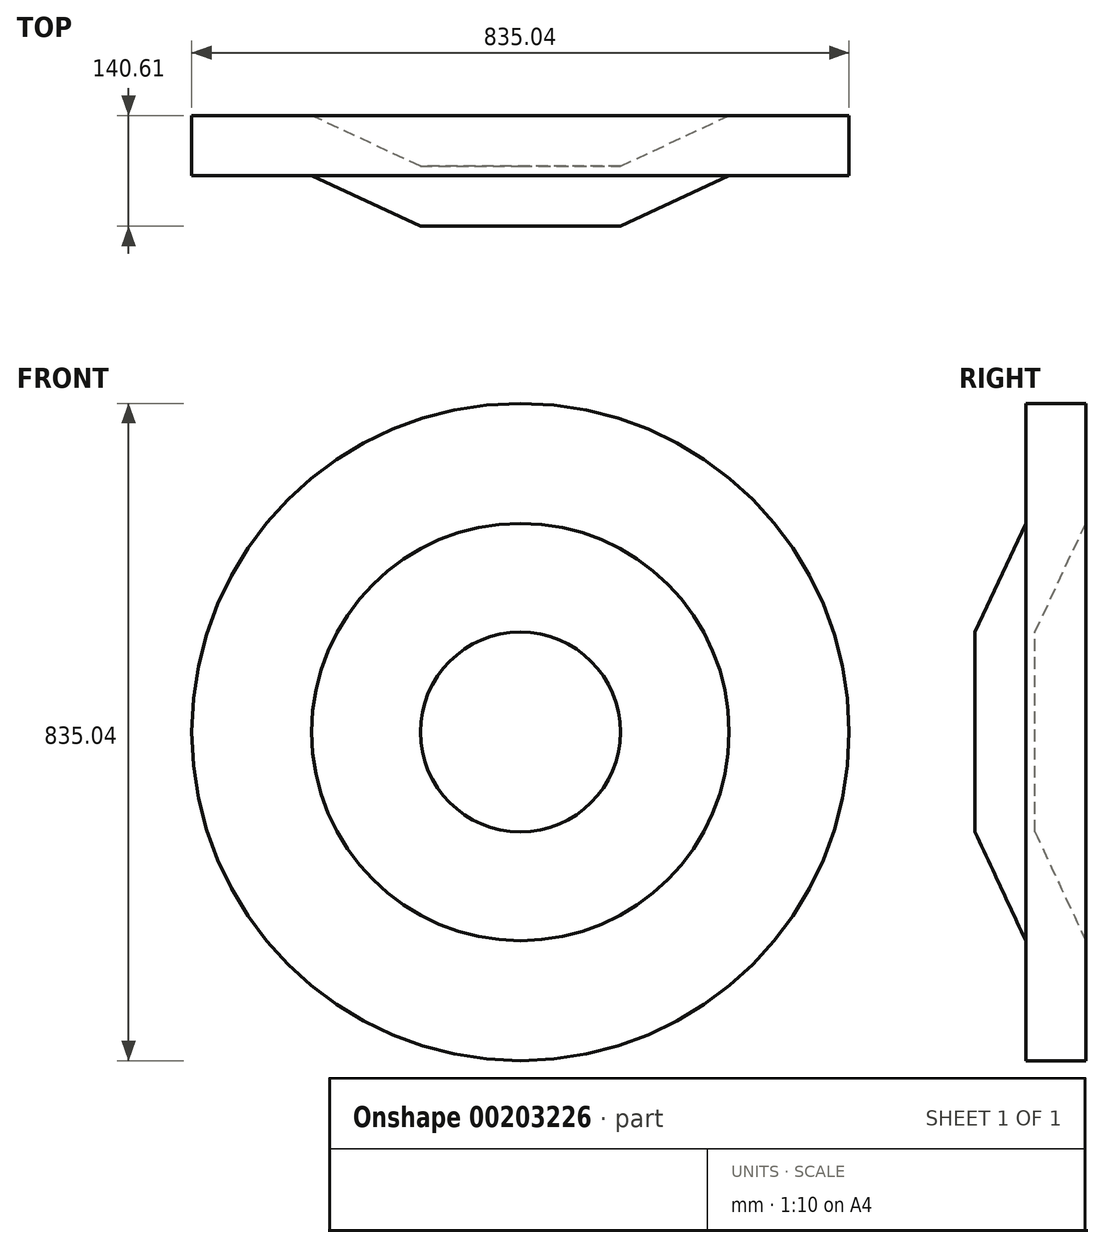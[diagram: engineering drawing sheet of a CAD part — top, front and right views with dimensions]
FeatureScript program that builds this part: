
annotation { "Feature Type Name" : "Feature", "Feature Type Description" : "" }
export const myFeature = defineFeature(function(context is Context, id is Id, definition is map)
    precondition{}
    {
        {
            var Q0;
            Q0=qCreatedBy(makeId("Top.planeOp"),FACE);
            var sketch = newSketch(context, id + "F0", { "sketchPlane" : qUnion([Q0])});
            skLineSegment(sketch, "E0.bottom", {"start": v(0, 0) * mm, "end": v(127, 0) * mm});
            skLineSegment(sketch, "E0.top", {"start": v(0, 76.2) * mm, "end": v(127, 76.2) * mm});
            skLineSegment(sketch, "E0.left", {"start": v(0, 0) * mm, "end": v(0, 76.2) * mm});
            skLineSegment(sketch, "E0.right", {"start": v(127, 0) * mm, "end": v(127, 76.2) * mm});
            skLineSegment(sketch, "E1", {"start": v(0, 76.2) * mm, "end": v(-138.12, 140.6) * mm});
            skLineSegment(sketch, "E2", {"start": v(0, 0) * mm, "end": v(-138.12, 64.4) * mm});
            skLineSegment(sketch, "E3.bottom", {"start": v(-138.12, 140.6) * mm, "end": v(-290.52, 140.6) * mm});
            skLineSegment(sketch, "E3.top", {"start": v(-138.12, 64.4) * mm, "end": v(-290.52, 64.4) * mm});
            skLineSegment(sketch, "E3.left", {"start": v(-138.12, 140.6) * mm, "end": v(-138.12, 64.4) * mm});
            skLineSegment(sketch, "E3.right", {"start": v(-290.52, 140.6) * mm, "end": v(-290.52, 64.4) * mm});
            skSolve(sketch);
        }
        {
            var Q0;
            Q0=makeQuery(id+"F0.imprint","IMPRINT",FACE,{"disambiguationData":[TD([[makeQuery(id+"F0.imprint","IMPRINT",EDGE,{"derivedFrom":sQuery(id+"F0.wireOp",EDGE,"E3.bottom")}),1.0]])]});
            var Q1;
            Q1=makeQuery(id+"F0.imprint","IMPRINT",FACE,{"disambiguationData":[TD([[makeQuery(id+"F0.imprint","IMPRINT",EDGE,{"derivedFrom":sQuery(id+"F0.wireOp",EDGE,"E0.left")}),1.0]])]});
            var Q2;
            Q2=makeQuery(id+"F0.imprint","IMPRINT",FACE,{"disambiguationData":[TD([[makeQuery(id+"F0.imprint","IMPRINT",EDGE,{"derivedFrom":sQuery(id+"F0.wireOp",EDGE,"E0.bottom")}),1.0]])]});
            var Q3;
            Q3=sQuery(id+"F0.wireOp",EDGE,"E0.right");
            revolve(context, id + "F1", {"entities" : qUnion([Q0, Q1, Q2]), "axis" : qUnion([Q3]), "revolveType" : RevolveType.FULL});
        }
    });
